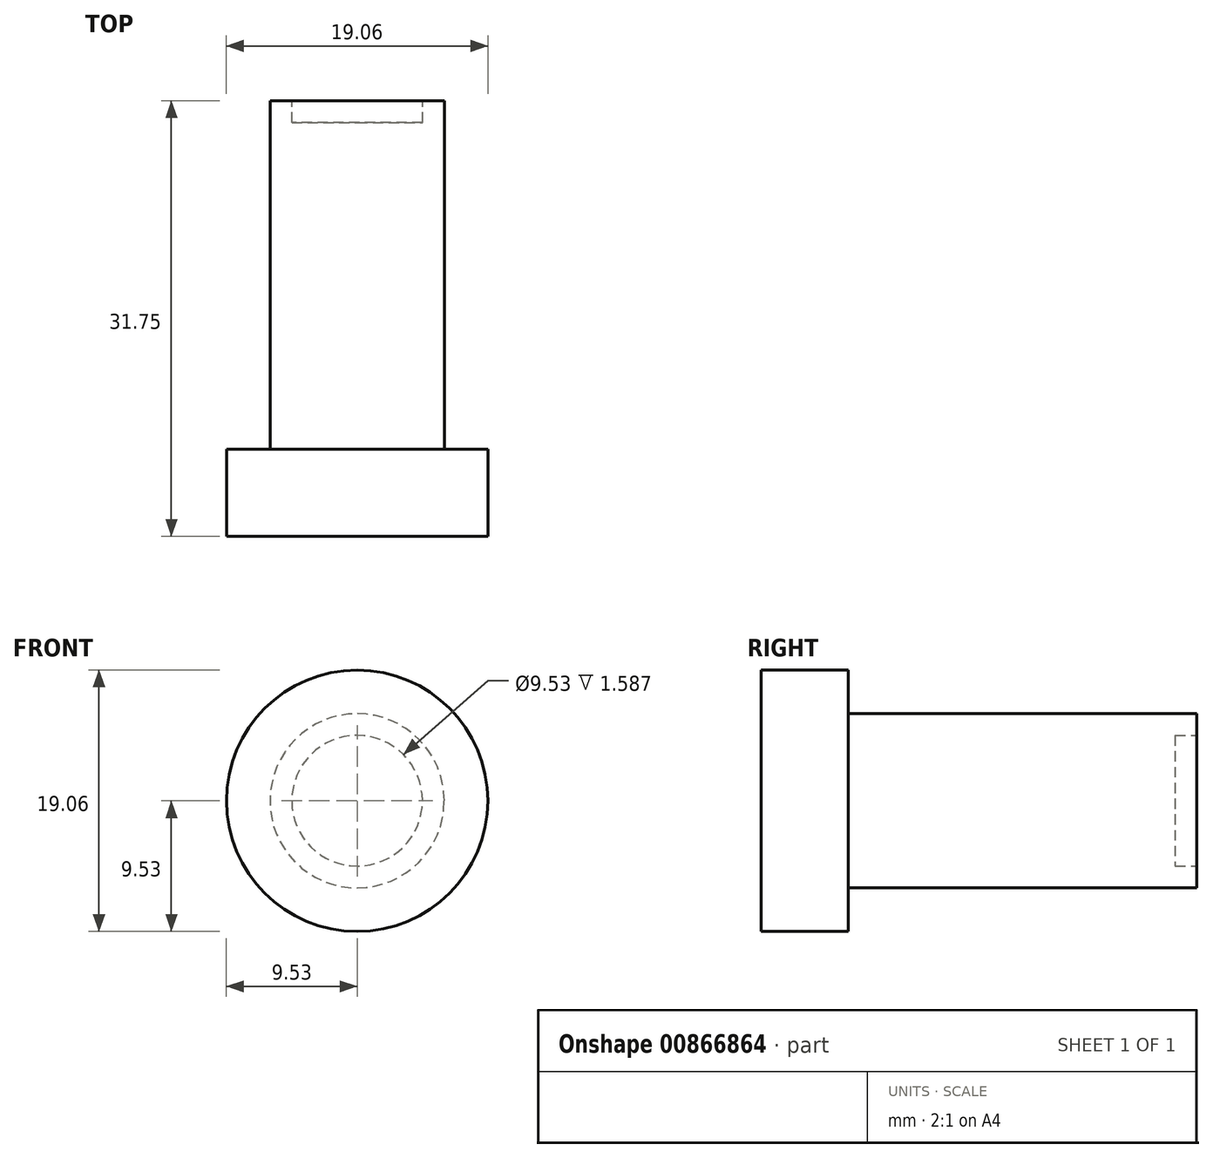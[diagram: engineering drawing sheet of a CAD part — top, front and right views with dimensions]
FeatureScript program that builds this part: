
annotation { "Feature Type Name" : "Feature", "Feature Type Description" : "" }
export const myFeature = defineFeature(function(context is Context, id is Id, definition is map)
    precondition{}
    {
        {
            var Q0;
            Q0=qCreatedBy(makeId("Front.planeOp"),FACE);
            var sketch = newSketch(context, id + "F0", { "sketchPlane" : qUnion([Q0])});
            skCircle(sketch, "E0", {"center": v(0, 0) * mm, "radius": 6.35 * mm});
            skSolve(sketch);
        }
        {
            var Q0;
            Q0=makeQuery(id+"F0.imprint","IMPRINT",FACE,{"disambiguationData":[TD([[makeQuery(id+"F0.imprint","IMPRINT",EDGE,{"derivedFrom":sQuery(id+"F0.wireOp",EDGE,"E0")}),1.0]])]});
            extrude(context, id + "F1", {"entities" : qUnion([Q0]), "depth" : 25.4 * mm, "offsetDistance" : 25.4 * mm});
        }
        {
            var Q0;
            Q0=makeQuery(id+"F1.opExtrude","CAP_FACE",FACE,{"disambiguationData":[OSD([sQuery(id+"F0.wireOp",EDGE,"E0")])],"isStart":true});
            var sketch = newSketch(context, id + "F2", { "sketchPlane" : qUnion([Q0])});
            skCircle(sketch, "E1", {"center": v(0, 0) * mm, "radius": 4.76 * mm});
            skSolve(sketch);
        }
        {
            var Q0;
            Q0 = qSketchRegion(id + "F2", true);
            extrude(context, id + "F3", {"entities" : qUnion([Q0]), "operationType" : NewBodyOperationType.REMOVE, "oppositeDirection" : true, "depth" : 1.59 * mm, "offsetDistance" : 25.4 * mm});
        }
        {
            var Q0;
            Q0=makeQuery(id+"F1.opExtrude","CAP_FACE",FACE,{"disambiguationData":[OSD([sQuery(id+"F0.wireOp",EDGE,"E0")])],"isStart":false});
            var sketch = newSketch(context, id + "F4", { "sketchPlane" : qUnion([Q0])});
            skCircle(sketch, "E2", {"center": v(0, 0) * mm, "radius": 9.53 * mm});
            skSolve(sketch);
        }
        {
            var Q0;
            Q0 = qSketchRegion(id + "F4", true);
            extrude(context, id + "F5", {"entities" : qUnion([Q0]), "operationType" : NewBodyOperationType.ADD, "depth" : 6.35 * mm, "offsetDistance" : 25.4 * mm});
        }
    });
